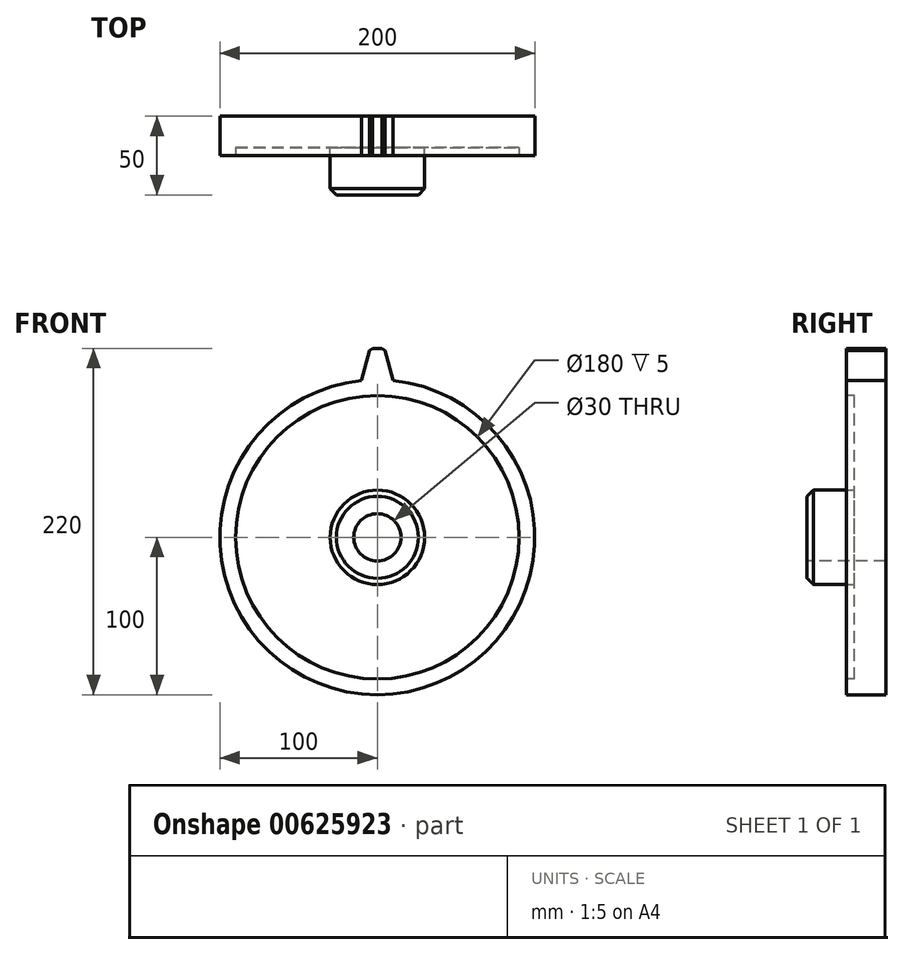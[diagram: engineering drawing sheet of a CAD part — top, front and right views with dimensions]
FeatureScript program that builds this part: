
annotation { "Feature Type Name" : "Feature", "Feature Type Description" : "" }
export const myFeature = defineFeature(function(context is Context, id is Id, definition is map)
    precondition{}
    {
        {
            var Q0;
            Q0=qCreatedBy(makeId("Front.planeOp"),FACE);
            var sketch = newSketch(context, id + "F0", { "sketchPlane" : qUnion([Q0])});
            skCircle(sketch, "E0", {"center": v(0, 0) * mm, "radius": 100 * mm});
            skSolve(sketch);
        }
        {
            var Q0;
            Q0=makeQuery(id+"F0.imprint","IMPRINT",FACE,{"disambiguationData":[TD([[makeQuery(id+"F0.imprint","IMPRINT",EDGE,{"derivedFrom":sQuery(id+"F0.wireOp",EDGE,"E0")}),1.0]])]});
            extrude(context, id + "F1", {"entities" : qUnion([Q0]), "depth" : 25 * mm, "offsetDistance" : 25 * mm});
        }
        {
            var Q0;
            Q0=qCreatedBy(makeId("Front.planeOp"),FACE);
            var sketch = newSketch(context, id + "F2", { "sketchPlane" : qUnion([Q0])});
            skLineSegment(sketch, "E1", {"start": v(-10, 99.5) * mm, "end": v(10, 99.5) * mm});
            skLineSegment(sketch, "E2", {"start": v(10, 99.5) * mm, "end": v(4.5, 120) * mm});
            skLineSegment(sketch, "E3", {"start": v(4.5, 120) * mm, "end": v(-4.5, 120) * mm});
            skLineSegment(sketch, "E4", {"start": v(-4.5, 120) * mm, "end": v(-10, 99.5) * mm});
            skSolve(sketch);
        }
        {
            var Q0;
            Q0=makeQuery(id+"F2.imprint","IMPRINT",FACE,{"disambiguationData":[TD([[makeQuery(id+"F2.imprint","IMPRINT",EDGE,{"derivedFrom":sQuery(id+"F2.wireOp",EDGE,"E1")}),1.0]])]});
            extrude(context, id + "F3", {"entities" : qUnion([Q0]), "operationType" : NewBodyOperationType.ADD, "depth" : 25 * mm, "offsetDistance" : 25 * mm});
        }
        {
            var Q0;
            Q0=makeQuery(id+"F3.opExtrude","SWEPT_EDGE",EDGE,{"disambiguationData":[OSD([sQuery(id+"F2.wireOp",EDGE,"E2"),sQuery(id+"F2.wireOp",EDGE,"E3")])]});
            var Q1;
            Q1=makeQuery(id+"F3.opExtrude","SWEPT_EDGE",EDGE,{"disambiguationData":[OSD([sQuery(id+"F2.wireOp",EDGE,"E3"),sQuery(id+"F2.wireOp",EDGE,"E4")])]});
            chamfer(context, id + "F4", {"entities" : qUnion([Q0, Q1]), "width" : 2 * mm, "tangentPropagation" : true});
        }
        {
            var Q0;
            Q0=makeQuery(id+"F3.opExtrude","SWEPT_EDGE",EDGE,{"disambiguationData":[OSD([sQuery(id+"F2.wireOp",EDGE,"E1"),sQuery(id+"F2.wireOp",EDGE,"E2")])]});
            var Q1;
            Q1=makeQuery(id+"F3.opExtrude","SWEPT_EDGE",EDGE,{"disambiguationData":[OSD([sQuery(id+"F2.wireOp",EDGE,"E1"),sQuery(id+"F2.wireOp",EDGE,"E4")])]});
            fillet(context, id + "F5", {"entities" : qUnion([Q0, Q1]), "radius" : 5 * mm, "tangentPropagation" : true, "allowEdgeOverflow" : false});
        }
        {
            var Q0;
            {var subQ0=sQuery(id+"F2.wireOp",EDGE,"E4");var subQ1=sQuery(id+"F2.wireOp",EDGE,"E3");var subQ2=sQuery(id+"F2.wireOp",EDGE,"E2");var subQ3=sQuery(id+"F2.wireOp",EDGE,"E1");Q0=makeQuery(id+"FIxAJ25CRCVRANu_1.19.F3.boolean.opBoolean","MERGE",FACE,{"derivedFrom":[makeQuery(id+"FIxAJ25CRCVRANu_1.18.F3.boolean.opBoolean","MERGE",FACE,{"derivedFrom":[makeQuery(id+"FIxAJ25CRCVRANu_1.17.F3.boolean.opBoolean","MERGE",FACE,{"derivedFrom":[makeQuery(id+"FIxAJ25CRCVRANu_1.16.F3.boolean.opBoolean","MERGE",FACE,{"derivedFrom":[makeQuery(id+"FIxAJ25CRCVRANu_1.15.F3.boolean.opBoolean","MERGE",FACE,{"derivedFrom":[makeQuery(id+"FIxAJ25CRCVRANu_1.14.F3.boolean.opBoolean","MERGE",FACE,{"derivedFrom":[makeQuery(id+"FIxAJ25CRCVRANu_1.13.F3.boolean.opBoolean","MERGE",FACE,{"derivedFrom":[makeQuery(id+"FIxAJ25CRCVRANu_1.12.F3.boolean.opBoolean","MERGE",FACE,{"derivedFrom":[makeQuery(id+"FIxAJ25CRCVRANu_1.11.F3.boolean.opBoolean","MERGE",FACE,{"derivedFrom":[makeQuery(id+"FIxAJ25CRCVRANu_1.10.F3.boolean.opBoolean","MERGE",FACE,{"derivedFrom":[makeQuery(id+"FIxAJ25CRCVRANu_1.9.F3.boolean.opBoolean","MERGE",FACE,{"derivedFrom":[makeQuery(id+"FIxAJ25CRCVRANu_1.8.F3.boolean.opBoolean","MERGE",FACE,{"derivedFrom":[makeQuery(id+"FIxAJ25CRCVRANu_1.7.F3.boolean.opBoolean","MERGE",FACE,{"derivedFrom":[makeQuery(id+"FIxAJ25CRCVRANu_1.6.F3.boolean.opBoolean","MERGE",FACE,{"derivedFrom":[makeQuery(id+"FIxAJ25CRCVRANu_1.5.F3.boolean.opBoolean","MERGE",FACE,{"derivedFrom":[makeQuery(id+"FIxAJ25CRCVRANu_1.4.F3.boolean.opBoolean","MERGE",FACE,{"derivedFrom":[makeQuery(id+"FIxAJ25CRCVRANu_1.3.F3.boolean.opBoolean","MERGE",FACE,{"derivedFrom":[makeQuery(id+"FIxAJ25CRCVRANu_1.2.F3.boolean.opBoolean","MERGE",FACE,{"derivedFrom":[makeQuery(id+"FIxAJ25CRCVRANu_1.1.F3.boolean.opBoolean","MERGE",FACE,{"derivedFrom":[makeQuery(id+"F3.boolean.opBoolean","MERGE",FACE,{"derivedFrom":[makeQuery(id+"F1.opExtrude","CAP_FACE",FACE,{"disambiguationData":[OSD([sQuery(id+"F0.wireOp",EDGE,"E0")])],"isStart":false}),makeQuery(id+"F3.opExtrude","CAP_FACE",FACE,{"disambiguationData":[OSD([subQ3,subQ2,subQ1,subQ0])],"isStart":false})]}),makeQuery(id+"FIxAJ25CRCVRANu_1.1.F3.opExtrude","CAP_FACE",FACE,{"disambiguationData":[OSD([subQ3,subQ2,subQ1,subQ0])],"isStart":false})]}),makeQuery(id+"FIxAJ25CRCVRANu_1.2.F3.opExtrude","CAP_FACE",FACE,{"disambiguationData":[OSD([subQ3,subQ2,subQ1,subQ0])],"isStart":false})]}),makeQuery(id+"FIxAJ25CRCVRANu_1.3.F3.opExtrude","CAP_FACE",FACE,{"disambiguationData":[OSD([subQ3,subQ2,subQ1,subQ0])],"isStart":false})]}),makeQuery(id+"FIxAJ25CRCVRANu_1.4.F3.opExtrude","CAP_FACE",FACE,{"disambiguationData":[OSD([subQ3,subQ2,subQ1,subQ0])],"isStart":false})]}),makeQuery(id+"FIxAJ25CRCVRANu_1.5.F3.opExtrude","CAP_FACE",FACE,{"disambiguationData":[OSD([subQ3,subQ2,subQ1,subQ0])],"isStart":false})]}),makeQuery(id+"FIxAJ25CRCVRANu_1.6.F3.opExtrude","CAP_FACE",FACE,{"disambiguationData":[OSD([subQ3,subQ2,subQ1,subQ0])],"isStart":false})]}),makeQuery(id+"FIxAJ25CRCVRANu_1.7.F3.opExtrude","CAP_FACE",FACE,{"disambiguationData":[OSD([subQ3,subQ2,subQ1,subQ0])],"isStart":false})]}),makeQuery(id+"FIxAJ25CRCVRANu_1.8.F3.opExtrude","CAP_FACE",FACE,{"disambiguationData":[OSD([subQ3,subQ2,subQ1,subQ0])],"isStart":false})]}),makeQuery(id+"FIxAJ25CRCVRANu_1.9.F3.opExtrude","CAP_FACE",FACE,{"disambiguationData":[OSD([subQ3,subQ2,subQ1,subQ0])],"isStart":false})]}),makeQuery(id+"FIxAJ25CRCVRANu_1.10.F3.opExtrude","CAP_FACE",FACE,{"disambiguationData":[OSD([subQ3,subQ2,subQ1,subQ0])],"isStart":false})]}),makeQuery(id+"FIxAJ25CRCVRANu_1.11.F3.opExtrude","CAP_FACE",FACE,{"disambiguationData":[OSD([subQ3,subQ2,subQ1,subQ0])],"isStart":false})]}),makeQuery(id+"FIxAJ25CRCVRANu_1.12.F3.opExtrude","CAP_FACE",FACE,{"disambiguationData":[OSD([subQ3,subQ2,subQ1,subQ0])],"isStart":false})]}),makeQuery(id+"FIxAJ25CRCVRANu_1.13.F3.opExtrude","CAP_FACE",FACE,{"disambiguationData":[OSD([subQ3,subQ2,subQ1,subQ0])],"isStart":false})]}),makeQuery(id+"FIxAJ25CRCVRANu_1.14.F3.opExtrude","CAP_FACE",FACE,{"disambiguationData":[OSD([subQ3,subQ2,subQ1,subQ0])],"isStart":false})]}),makeQuery(id+"FIxAJ25CRCVRANu_1.15.F3.opExtrude","CAP_FACE",FACE,{"disambiguationData":[OSD([subQ3,subQ2,subQ1,subQ0])],"isStart":false})]}),makeQuery(id+"FIxAJ25CRCVRANu_1.16.F3.opExtrude","CAP_FACE",FACE,{"disambiguationData":[OSD([subQ3,subQ2,subQ1,subQ0])],"isStart":false})]}),makeQuery(id+"FIxAJ25CRCVRANu_1.17.F3.opExtrude","CAP_FACE",FACE,{"disambiguationData":[OSD([subQ3,subQ2,subQ1,subQ0])],"isStart":false})]}),makeQuery(id+"FIxAJ25CRCVRANu_1.18.F3.opExtrude","CAP_FACE",FACE,{"disambiguationData":[OSD([subQ3,subQ2,subQ1,subQ0])],"isStart":false})]}),makeQuery(id+"FIxAJ25CRCVRANu_1.19.F3.opExtrude","CAP_FACE",FACE,{"disambiguationData":[OSD([subQ3,subQ2,subQ1,subQ0])],"isStart":false})]});}
            var sketch = newSketch(context, id + "F6", { "sketchPlane" : qUnion([Q0])});
            skCircle(sketch, "E5", {"center": v(0, 0) * mm, "radius": 90 * mm});
            skSolve(sketch);
        }
        {
            var Q0;
            Q0=makeQuery(id+"F6.imprint","IMPRINT",FACE,{"disambiguationData":[TD([[makeQuery(id+"F6.imprint","IMPRINT",EDGE,{"derivedFrom":sQuery(id+"F6.wireOp",EDGE,"E5")}),1.0]])]});
            extrude(context, id + "F7", {"entities" : qUnion([Q0]), "operationType" : NewBodyOperationType.REMOVE, "oppositeDirection" : true, "depth" : 5 * mm, "offsetDistance" : 25 * mm});
        }
        {
            var Q0;
            Q0=makeQuery(id+"F7.boolean.opBoolean","COPY",FACE,{"derivedFrom":makeQuery(id+"F7.opExtrude","CAP_FACE",FACE,{"disambiguationData":[OSD([sQuery(id+"F6.wireOp",EDGE,"E5")])],"isStart":false})});
            var sketch = newSketch(context, id + "F8", { "sketchPlane" : qUnion([Q0])});
            skCircle(sketch, "E6", {"center": v(0, 0) * mm, "radius": 30 * mm});
            skSolve(sketch);
        }
        {
            var Q0;
            Q0=makeQuery(id+"F8.imprint","IMPRINT",FACE,{"disambiguationData":[TD([[makeQuery(id+"F8.imprint","IMPRINT",EDGE,{"derivedFrom":sQuery(id+"F8.wireOp",EDGE,"E6")}),1.0]])]});
            extrude(context, id + "F9", {"entities" : qUnion([Q0]), "operationType" : NewBodyOperationType.ADD, "depth" : 30 * mm, "offsetDistance" : 25 * mm});
        }
        {
            var Q0;
            Q0=makeQuery(id+"F9.opExtrude","CAP_FACE",FACE,{"disambiguationData":[OSD([sQuery(id+"F8.wireOp",EDGE,"E6")])],"isStart":false});
            var sketch = newSketch(context, id + "F10", { "sketchPlane" : qUnion([Q0])});
            skCircle(sketch, "E7", {"center": v(0, 0) * mm, "radius": 15 * mm});
            skSolve(sketch);
        }
        {
            var Q0;
            Q0=makeQuery(id+"F10.imprint","IMPRINT",FACE,{"disambiguationData":[TD([[makeQuery(id+"F10.imprint","IMPRINT",EDGE,{"derivedFrom":sQuery(id+"F10.wireOp",EDGE,"E7")}),1.0]])]});
            extrude(context, id + "F11", {"entities" : qUnion([Q0]), "operationType" : NewBodyOperationType.REMOVE, "endBound" : BoundingType.UP_TO_NEXT, "oppositeDirection" : true, "depth" : 25 * mm, "offsetDistance" : 25 * mm});
        }
        {
            var Q0;
            Q0=makeQuery(id+"F9.opExtrude","CAP_EDGE",EDGE,{"disambiguationData":[OSD([sQuery(id+"F8.wireOp",EDGE,"E6")])],"isStart":false});
            var Q1;
            Q1=makeQuery(id+"F11.boolean.opBoolean","COPY",EDGE,{"derivedFrom":makeQuery(id+"F11.opExtrude","CAP_EDGE",EDGE,{"disambiguationData":[OSD([sQuery(id+"F10.wireOp",EDGE,"E7")])],"isStart":true})});
            chamfer(context, id + "F12", {"entities" : qUnion([Q0, Q1]), "width" : 4 * mm, "tangentPropagation" : true});
        }
    });
